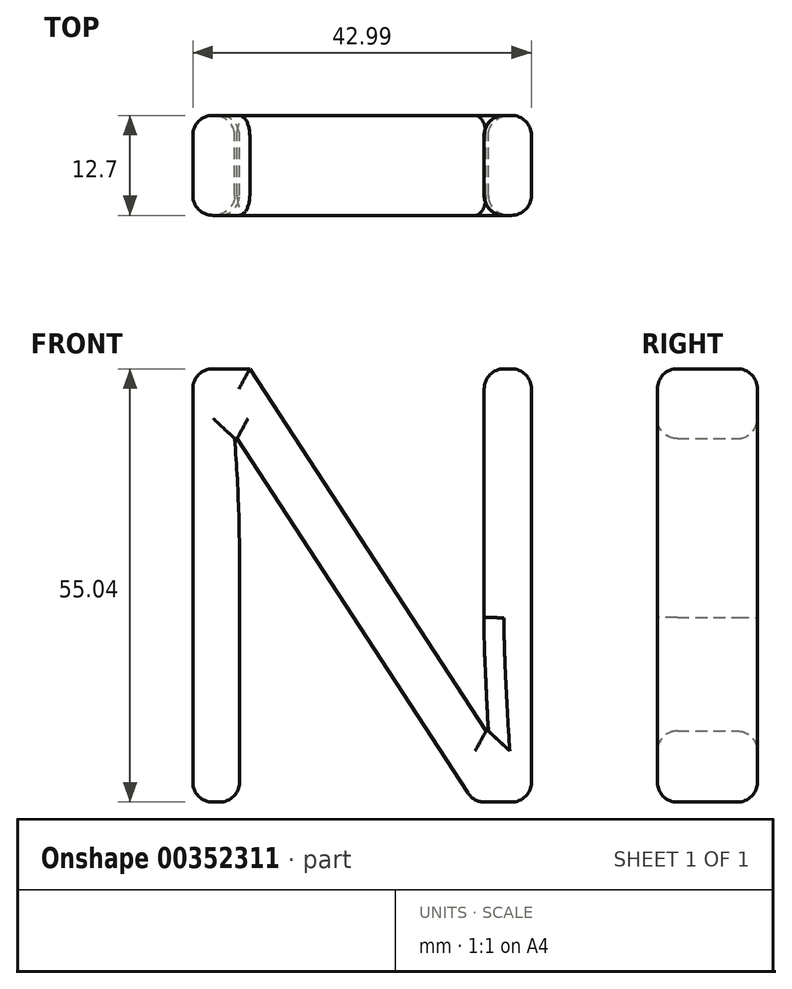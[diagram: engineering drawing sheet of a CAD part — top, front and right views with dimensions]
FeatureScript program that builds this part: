
annotation { "Feature Type Name" : "Feature", "Feature Type Description" : "" }
export const myFeature = defineFeature(function(context is Context, id is Id, definition is map)
    precondition{}
    {
        {
            var Q0;
            Q0=qCreatedBy(makeId("Front.planeOp"),FACE);
            var sketch = newSketch(context, id + "F0", { "sketchPlane" : qUnion([Q0])});
            skText(sketch, "E0", { "text": "N", "fontName": "OpenSans-Regular.ttf"});
            const initialGuessF0  = {"E0": [-0.02719, -0.02988, 1, 0, 0.05551]};
            skSetInitialGuess(sketch, initialGuessF0);
            skSolve(sketch);
        }
        {
            var Q0;
            Q0=makeQuery(id+"F0.imprint","IMPRINT",FACE,{"disambiguationData":[TD([[makeQuery(id+"F0.imprint","IMPRINT",EDGE,{"derivedFrom":sQuery(id+"F0.wireOp",EDGE,"E0.sketch_text.stroke-0")}),-1.0]])]});
            extrude(context, id + "F1", {"entities" : qUnion([Q0]), "depth" : 12.7 * mm});
        }
        {
            var Q0;
            Q0=makeQuery(id+"F1.opExtrude","CAP_EDGE",EDGE,{"disambiguationData":[OSD([sQuery(id+"F0.wireOp",EDGE,"E0.sketch_text.stroke-1")])],"isStart":true});
            var Q1;
            Q1=makeQuery(id+"F1.opExtrude","CAP_EDGE",EDGE,{"disambiguationData":[OSD([sQuery(id+"F0.wireOp",EDGE,"E0.sketch_text.stroke-8")])],"isStart":true});
            var Q2;
            Q2=makeQuery(id+"F1.opExtrude","CAP_EDGE",EDGE,{"disambiguationData":[OSD([sQuery(id+"F0.wireOp",EDGE,"E0.sketch_text.stroke-4")])],"isStart":true});
            var Q3;
            Q3=makeQuery(id+"F1.opExtrude","CAP_EDGE",EDGE,{"disambiguationData":[OSD([sQuery(id+"F0.wireOp",EDGE,"E0.sketch_text.stroke-6")])],"isStart":true});
            var Q4;
            Q4=makeQuery(id+"F1.opExtrude","CAP_EDGE",EDGE,{"disambiguationData":[OSD([sQuery(id+"F0.wireOp",EDGE,"E0.sketch_text.stroke-14")])],"isStart":true});
            var Q5;
            Q5=makeQuery(id+"F1.opExtrude","CAP_EDGE",EDGE,{"disambiguationData":[OSD([sQuery(id+"F0.wireOp",EDGE,"E0.sketch_text.stroke-10")])],"isStart":true});
            var Q6;
            Q6=makeQuery(id+"F1.opExtrude","SWEPT_EDGE",EDGE,{"disambiguationData":[OSD([sQuery(id+"F0.wireOp",EDGE,"E0.sketch_text.stroke-4"),sQuery(id+"F0.wireOp",EDGE,"E0.sketch_text.stroke-5")])]});
            var Q7;
            Q7=makeQuery(id+"F1.opExtrude","CAP_EDGE",EDGE,{"disambiguationData":[OSD([sQuery(id+"F0.wireOp",EDGE,"E0.sketch_text.stroke-4")])],"isStart":false});
            var Q8;
            Q8=makeQuery(id+"F1.opExtrude","CAP_EDGE",EDGE,{"disambiguationData":[OSD([sQuery(id+"F0.wireOp",EDGE,"E0.sketch_text.stroke-14")])],"isStart":false});
            var Q9;
            Q9=makeQuery(id+"F1.opExtrude","SWEPT_EDGE",EDGE,{"disambiguationData":[OSD([sQuery(id+"F0.wireOp",EDGE,"E0.sketch_text.stroke-0"),sQuery(id+"F0.wireOp",EDGE,"E0.sketch_text.stroke-14")])]});
            var Q10;
            Q10=makeQuery(id+"F1.opExtrude","SWEPT_EDGE",EDGE,{"disambiguationData":[OSD([sQuery(id+"F0.wireOp",EDGE,"E0.sketch_text.stroke-13"),sQuery(id+"F0.wireOp",EDGE,"E0.sketch_text.stroke-14")])]});
            var Q11;
            Q11=makeQuery(id+"F1.opExtrude","CAP_EDGE",EDGE,{"disambiguationData":[OSD([sQuery(id+"F0.wireOp",EDGE,"E0.sketch_text.stroke-13")])],"isStart":true});
            var Q12;
            Q12=makeQuery(id+"F1.opExtrude","SWEPT_EDGE",EDGE,{"disambiguationData":[OSD([sQuery(id+"F0.wireOp",EDGE,"E0.sketch_text.stroke-0"),sQuery(id+"F0.wireOp",EDGE,"E0.sketch_text.stroke-1")])]});
            var Q13;
            Q13=makeQuery(id+"F1.opExtrude","CAP_EDGE",EDGE,{"disambiguationData":[OSD([sQuery(id+"F0.wireOp",EDGE,"E0.sketch_text.stroke-1")])],"isStart":false});
            var Q14;
            Q14=makeQuery(id+"F1.opExtrude","CAP_EDGE",EDGE,{"disambiguationData":[OSD([sQuery(id+"F0.wireOp",EDGE,"E0.sketch_text.stroke-6")])],"isStart":false});
            var Q15;
            Q15=makeQuery(id+"F1.opExtrude","SWEPT_EDGE",EDGE,{"disambiguationData":[OSD([sQuery(id+"F0.wireOp",EDGE,"E0.sketch_text.stroke-5"),sQuery(id+"F0.wireOp",EDGE,"E0.sketch_text.stroke-6")])]});
            var Q16;
            Q16=makeQuery(id+"F1.opExtrude","SWEPT_EDGE",EDGE,{"disambiguationData":[OSD([sQuery(id+"F0.wireOp",EDGE,"E0.sketch_text.stroke-6"),sQuery(id+"F0.wireOp",EDGE,"E0.sketch_text.stroke-7")])]});
            var Q17;
            Q17=makeQuery(id+"F1.opExtrude","CAP_EDGE",EDGE,{"disambiguationData":[OSD([sQuery(id+"F0.wireOp",EDGE,"E0.sketch_text.stroke-7")])],"isStart":true});
            var Q18;
            Q18=makeQuery(id+"F1.opExtrude","SWEPT_EDGE",EDGE,{"disambiguationData":[OSD([sQuery(id+"F0.wireOp",EDGE,"E0.sketch_text.stroke-12"),sQuery(id+"F0.wireOp",EDGE,"E0.sketch_text.stroke-13")])]});
            var Q19;
            Q19=makeQuery(id+"F1.opExtrude","CAP_EDGE",EDGE,{"disambiguationData":[OSD([sQuery(id+"F0.wireOp",EDGE,"E0.sketch_text.stroke-8")])],"isStart":false});
            var Q20;
            Q20=makeQuery(id+"F1.opExtrude","CAP_EDGE",EDGE,{"disambiguationData":[OSD([sQuery(id+"F0.wireOp",EDGE,"E0.sketch_text.stroke-7")])],"isStart":false});
            var Q21;
            Q21=makeQuery(id+"F1.opExtrude","CAP_EDGE",EDGE,{"disambiguationData":[OSD([sQuery(id+"F0.wireOp",EDGE,"E0.sketch_text.stroke-12")])],"isStart":false});
            var Q22;
            Q22=makeQuery(id+"F1.opExtrude","CAP_EDGE",EDGE,{"disambiguationData":[OSD([sQuery(id+"F0.wireOp",EDGE,"E0.sketch_text.stroke-11")])],"isStart":false});
            var Q23;
            Q23=makeQuery(id+"F1.opExtrude","CAP_EDGE",EDGE,{"disambiguationData":[OSD([sQuery(id+"F0.wireOp",EDGE,"E0.sketch_text.stroke-3")])],"isStart":false});
            var Q24;
            Q24=makeQuery(id+"F1.opExtrude","CAP_FACE",FACE,{"disambiguationData":[OSD([sQuery(id+"F0.wireOp",EDGE,"E0.sketch_text.stroke-0"),sQuery(id+"F0.wireOp",EDGE,"E0.sketch_text.stroke-1"),sQuery(id+"F0.wireOp",EDGE,"E0.sketch_text.stroke-2"),sQuery(id+"F0.wireOp",EDGE,"E0.sketch_text.stroke-3"),sQuery(id+"F0.wireOp",EDGE,"E0.sketch_text.stroke-4"),sQuery(id+"F0.wireOp",EDGE,"E0.sketch_text.stroke-5"),sQuery(id+"F0.wireOp",EDGE,"E0.sketch_text.stroke-6"),sQuery(id+"F0.wireOp",EDGE,"E0.sketch_text.stroke-7"),sQuery(id+"F0.wireOp",EDGE,"E0.sketch_text.stroke-8"),sQuery(id+"F0.wireOp",EDGE,"E0.sketch_text.stroke-9"),sQuery(id+"F0.wireOp",EDGE,"E0.sketch_text.stroke-10"),sQuery(id+"F0.wireOp",EDGE,"E0.sketch_text.stroke-11"),sQuery(id+"F0.wireOp",EDGE,"E0.sketch_text.stroke-12"),sQuery(id+"F0.wireOp",EDGE,"E0.sketch_text.stroke-13"),sQuery(id+"F0.wireOp",EDGE,"E0.sketch_text.stroke-14")])],"isStart":false});
            var Q25;
            Q25=makeQuery(id+"F1.opExtrude","CAP_FACE",FACE,{"disambiguationData":[OSD([sQuery(id+"F0.wireOp",EDGE,"E0.sketch_text.stroke-0"),sQuery(id+"F0.wireOp",EDGE,"E0.sketch_text.stroke-1"),sQuery(id+"F0.wireOp",EDGE,"E0.sketch_text.stroke-2"),sQuery(id+"F0.wireOp",EDGE,"E0.sketch_text.stroke-3"),sQuery(id+"F0.wireOp",EDGE,"E0.sketch_text.stroke-4"),sQuery(id+"F0.wireOp",EDGE,"E0.sketch_text.stroke-5"),sQuery(id+"F0.wireOp",EDGE,"E0.sketch_text.stroke-6"),sQuery(id+"F0.wireOp",EDGE,"E0.sketch_text.stroke-7"),sQuery(id+"F0.wireOp",EDGE,"E0.sketch_text.stroke-8"),sQuery(id+"F0.wireOp",EDGE,"E0.sketch_text.stroke-9"),sQuery(id+"F0.wireOp",EDGE,"E0.sketch_text.stroke-10"),sQuery(id+"F0.wireOp",EDGE,"E0.sketch_text.stroke-11"),sQuery(id+"F0.wireOp",EDGE,"E0.sketch_text.stroke-12"),sQuery(id+"F0.wireOp",EDGE,"E0.sketch_text.stroke-13"),sQuery(id+"F0.wireOp",EDGE,"E0.sketch_text.stroke-14")])],"isStart":true});
            fillet(context, id + "F2", {"entities" : qUnion([Q0, Q1, Q2, Q3, Q4, Q5, Q6, Q7, Q8, Q9, Q10, Q11, Q12, Q13, Q14, Q15, Q16, Q17, Q18, Q19, Q20, Q21, Q22, Q23, Q24, Q25]), "radius" : 2.54 * mm, "tangentPropagation" : true, "allowEdgeOverflow" : false});
        }
    });
